# Revit family: Sink-Top_Mount-Kitchen-KOHLER-Deerfield-K-5873_1
name_source: partatom
category: Plumbing Fixtures
units: mm (PartAtom-declared; Revit-internal decimal feet)

## family parameters
Cut with Voids When Loaded = No
Host = Face
OmniClass Number = 23.31.13.00
OmniClass Title = Sinks
Part Type = Normal
Room Calculation Point = No
Round Connector Dimension = Use Diameter
Shared = No

## types (3) — shared parameters
ADA Compliant = No
Assembly Code = D2010400
CW Connection = No
Cold Water Inlet = Cold Water Inlet
Date Modified = 08/30/2022
Default Elevation = 36"
Description = 33 inch x 22 inch x 9-5/8 inch top-mount double-equal kitchen sink
Drain Included = No
HW Connection = No
Height = 9 5/8"
Hot Water Inlet = Hot Water Inlet
Length = 33"
Manufacturer = Kohler Co.
Master Format 2014 = 22 41 16
Master Format 2014 Name = Residential Lavatories and Sinks
Material = Enameled Cast Iron
Product Documentation Link = https://www.us.kohler.com
Product Name = Deerfield
Product Page URL = http://www.us.kohler.com
URL = https://www.us.kohler.com
Vent Connection = No
Waste Connection = Yes
Waste Water Outlet 1 = Waste Water Outlet 1
Waste Water Outlet 2 = Waste Water Outlet 2
WaterSense Certified = No
Width = 22"

## per-type parameters (varying)
| type | Finish | Model | Type |
| 0-White | KOHLER-Enameled_Cast_Iron-0-White | K-5873-1-0 | 1 |
| 96-Biscuit | KOHLER-Enameled_Cast_Iron-96-Biscuit | K-5873-1-96 | 3 |
| 7-Black Black | KOHLER-Enameled_Cast_Iron-7-Black_Black | K-5873-1-7 | 2 |

## geometry (parser evidence)
native form markers: Sweep x5
no freeform markers — native parametric forms only
